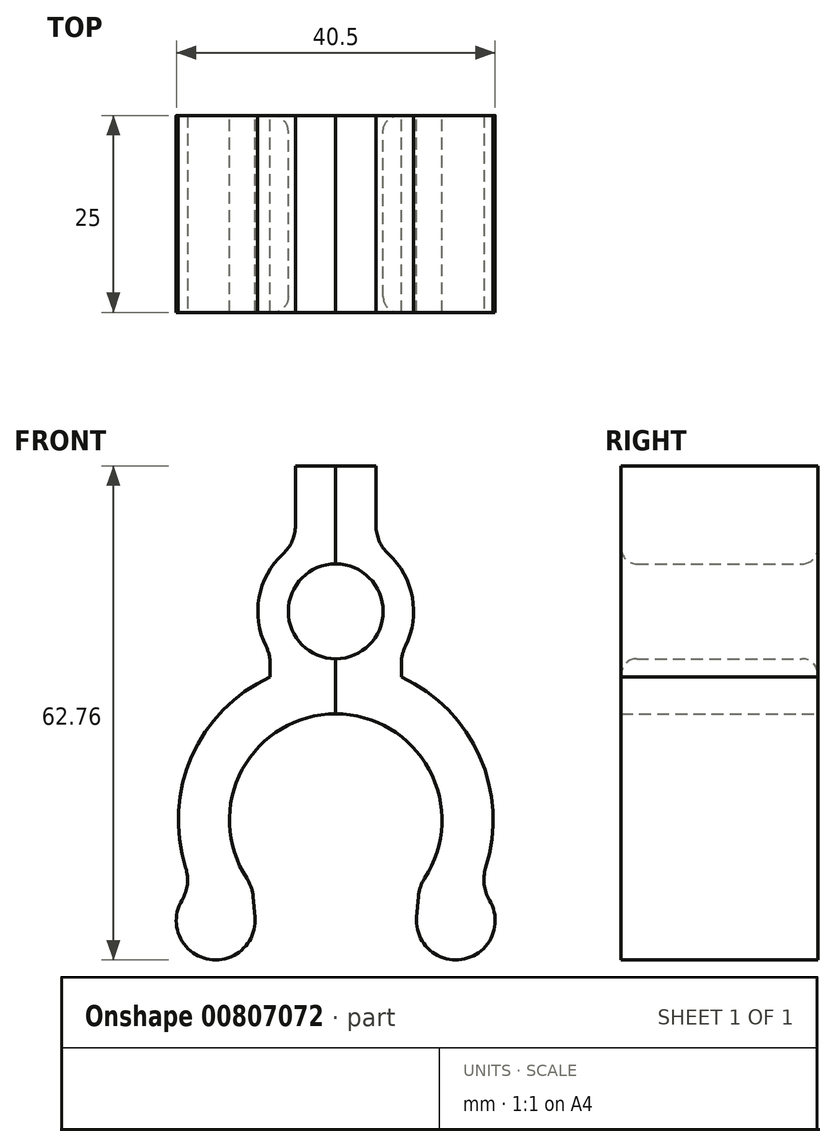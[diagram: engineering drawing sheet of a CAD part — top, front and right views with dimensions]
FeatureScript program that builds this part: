
annotation { "Feature Type Name" : "Feature", "Feature Type Description" : "" }
export const myFeature = defineFeature(function(context is Context, id is Id, definition is map)
    precondition{}
    {
        {
            var Q0;
            Q0=qCreatedBy(makeId("Front.planeOp"),FACE);
            var sketch = newSketch(context, id + "F0", { "sketchPlane" : qUnion([Q0])});
            skLineSegment(sketch, "E0", {"start": v(10.61, -34.87) * mm, "end": v(10.27, -38.85) * mm});
            skArc(sketch, "E1", {"start": v(10.27, -38.85) * mm, "mid": v(17.41, -43.8) * mm, "end": v(18.05, -35.14) * mm});
            skArc(sketch, "E2", {"start": v(8.33, -5.34) * mm, "mid": v(9.64, 2.25) * mm, "end": v(5.11, 8.48) * mm});
            skArc(sketch, "E3", {"start": v(0, -6.02) * mm, "mid": v(6.02, 0) * mm, "end": v(0, 6.02) * mm});
            skPoint(sketch, "E4.end.orphan", {"position": v(5.11, 0) * mm});
            skLineSegment(sketch, "E5", {"start": v(0, 71.13) * mm, "end": v(0, -72.93) * mm, "construction": true});
            skLineSegment(sketch, "E6", {"start": v(5.11, 8.48) * mm, "end": v(5.11, 18.48) * mm});
            skLineSegment(sketch, "E7", {"start": v(0.13, 84.1) * mm, "end": v(0, 71.13) * mm, "construction": true});
            skLineSegment(sketch, "E8", {"start": v(5.11, 18.48) * mm, "end": v(0, 18.48) * mm});
            skLineSegment(sketch, "E9", {"start": v(0, 18.48) * mm, "end": v(0, 6.02) * mm});
            skLineSegment(sketch, "E10", {"start": v(0, -6.02) * mm, "end": v(0, -26.52) * mm});
            skArc(sketch, "E11", {"start": v(10.61, -34.87) * mm, "mid": v(12.14, -20.63) * mm, "end": v(0, -13.02) * mm});
            skLineSegment(sketch, "E12", {"start": v(8.33, -5.34) * mm, "end": v(8.33, -8.34) * mm});
            skArc(sketch, "E13", {"start": v(18.05, -35.14) * mm, "mid": v(18.8, -19.7) * mm, "end": v(8.33, -8.34) * mm});
            skSolve(sketch);
        }
        {
            var Q0;
            Q0=qSketchRegion(id+"F0",true);
            extrude(context, id + "F1", {"entities" : qUnion([Q0]), "depth" : 25 * mm, "offsetDistance" : 25 * mm});
        }
        {
            var Q0;
            Q0=makeQuery(id+"F1.opExtrude","SWEPT_BODY",BODY,{"disambiguationData":[OSD([sQuery(id+"F0.wireOp",EDGE,"cfabb739-dba9-4975-bd49-091e3b57f569"),sQuery(id+"F0.wireOp",EDGE,"5847780e-0f5a-4472-9120-1fdb006a39dd"),sQuery(id+"F0.wireOp",EDGE,"E0"),sQuery(id+"F0.wireOp",EDGE,"E1"),sQuery(id+"F0.wireOp",EDGE,"E2"),sQuery(id+"F0.wireOp",EDGE,"E3"),sQuery(id+"F0.wireOp",EDGE,"LwMaPAxc-ASng-TWKL-FKsP-XUbiFX4LCitD"),sQuery(id+"F0.wireOp",EDGE,"E6"),sQuery(id+"F0.wireOp",EDGE,"E8"),sQuery(id+"F0.wireOp",EDGE,"E9"),sQuery(id+"F0.wireOp",EDGE,"E10")])]});
            var Q1;
            Q1=qCreatedBy(makeId("Right.planeOp"),FACE);
            mirror(context, id + "F2", {"entities" : qUnion([Q0]), "mirrorPlane" : qUnion([Q1])});
        }
        {
            var Q0;
            Q0=makeQuery(id+"F1.opExtrude","SWEPT_EDGE",EDGE,{"disambiguationData":[OSD([sQuery(id+"F0.wireOp",EDGE,"E0"),sQuery(id+"F0.wireOp",EDGE,"E11")])]});
            var Q1;
            Q1=makeQuery(id+"F2.opPattern","COPY",EDGE,{"derivedFrom":makeQuery(id+"F1.opExtrude","SWEPT_EDGE",EDGE,{"disambiguationData":[OSD([sQuery(id+"F0.wireOp",EDGE,"E0"),sQuery(id+"F0.wireOp",EDGE,"E11")])]}),"instanceName":"1"});
            var Q2;
            Q2=makeQuery(id+"F2.opPattern","COPY",EDGE,{"derivedFrom":makeQuery(id+"F1.opExtrude","SWEPT_EDGE",EDGE,{"disambiguationData":[OSD([sQuery(id+"F0.wireOp",EDGE,"E1"),sQuery(id+"F0.wireOp",EDGE,"E13")])]}),"instanceName":"1"});
            var Q3;
            Q3=makeQuery(id+"F1.opExtrude","SWEPT_EDGE",EDGE,{"disambiguationData":[OSD([sQuery(id+"F0.wireOp",EDGE,"E1"),sQuery(id+"F0.wireOp",EDGE,"E13")])]});
            var Q4;
            Q4=makeQuery(id+"F2.opPattern","COPY",EDGE,{"derivedFrom":makeQuery(id+"F1.opExtrude","SWEPT_EDGE",EDGE,{"disambiguationData":[OSD([sQuery(id+"F0.wireOp",EDGE,"E2"),sQuery(id+"F0.wireOp",EDGE,"E6")])]}),"instanceName":"1"});
            var Q5;
            Q5=makeQuery(id+"F2.opPattern","COPY",EDGE,{"derivedFrom":makeQuery(id+"F1.opExtrude","SWEPT_EDGE",EDGE,{"disambiguationData":[OSD([sQuery(id+"F0.wireOp",EDGE,"E2"),sQuery(id+"F0.wireOp",EDGE,"E12")])]}),"instanceName":"1"});
            var Q6;
            Q6=makeQuery(id+"F1.opExtrude","SWEPT_EDGE",EDGE,{"disambiguationData":[OSD([sQuery(id+"F0.wireOp",EDGE,"E2"),sQuery(id+"F0.wireOp",EDGE,"E6")])]});
            var Q7;
            Q7=makeQuery(id+"F1.opExtrude","SWEPT_EDGE",EDGE,{"disambiguationData":[OSD([sQuery(id+"F0.wireOp",EDGE,"E2"),sQuery(id+"F0.wireOp",EDGE,"E12")])]});
            var Q8;
            Q8=makeQuery(id+"F2.opPattern","COPY",EDGE,{"derivedFrom":makeQuery(id+"Fz5VlACo7VjdTQA_1.opExtrude","SWEPT_EDGE",EDGE,{"disambiguationData":[OSD([sQuery(id+"FI2dAfJpOKtGOTZ_1.wireOp",EDGE,"UufLFT2Z-upBZ-YC00-3sW9-ZrS4UPln2tA3"),sQuery(id+"FI2dAfJpOKtGOTZ_1.wireOp",EDGE,"f7488829-f30d-4c1d-9d05-a88ade316224.trimOffspring")])]}),"instanceName":"1"});
            var Q9;
            Q9=makeQuery(id+"F2.opPattern","COPY",EDGE,{"derivedFrom":makeQuery(id+"Fz5VlACo7VjdTQA_1.opExtrude","SWEPT_EDGE",EDGE,{"disambiguationData":[OSD([sQuery(id+"FI2dAfJpOKtGOTZ_1.wireOp",EDGE,"82edda89-2339-4690-89e7-abee45e1404a.trimOffspring"),sQuery(id+"FI2dAfJpOKtGOTZ_1.wireOp",EDGE,"e6c82897-9f81-4bd0-b549-450949e90f70.trimOffspring")])]}),"instanceName":"1"});
            var Q10;
            Q10=makeQuery(id+"F2.opPattern","COPY",EDGE,{"derivedFrom":makeQuery(id+"Fz5VlACo7VjdTQA_1.opExtrude","SWEPT_EDGE",EDGE,{"disambiguationData":[OSD([sQuery(id+"FI2dAfJpOKtGOTZ_1.wireOp",EDGE,"dAwRz9Mk-8VAy-pzP0-fNDg-vniHaInSBWGX"),sQuery(id+"FI2dAfJpOKtGOTZ_1.wireOp",EDGE,"3f8ad037-8f99-422e-a5f7-4226f7c6d37a0.MirrorCS")])]}),"instanceName":"1"});
            var Q11;
            Q11=makeQuery(id+"Fz5VlACo7VjdTQA_1.opExtrude","SWEPT_EDGE",EDGE,{"disambiguationData":[OSD([sQuery(id+"FI2dAfJpOKtGOTZ_1.wireOp",EDGE,"dAwRz9Mk-8VAy-pzP0-fNDg-vniHaInSBWGX"),sQuery(id+"FI2dAfJpOKtGOTZ_1.wireOp",EDGE,"o45zF1qc-RgXT-cvMq-ReTE-ZHE0aTBPM8XX")])]});
            fillet(context, id + "F3", {"entities" : qUnion([Q0, Q1, Q2, Q3, Q4, Q5, Q6, Q7, Q8, Q9, Q10, Q11]), "radius" : 5 * mm, "tangentPropagation" : true, "allowEdgeOverflow" : false});
        }
        {
            var Q0;
            Q0=makeQuery(id+"F1.opExtrude","CAP_EDGE",EDGE,{"disambiguationData":[OSD([sQuery(id+"F0.wireOp",EDGE,"E3")])],"isStart":false});
            var Q1;
            Q1=makeQuery(id+"F2.opPattern","COPY",EDGE,{"derivedFrom":makeQuery(id+"F1.opExtrude","CAP_EDGE",EDGE,{"disambiguationData":[OSD([sQuery(id+"F0.wireOp",EDGE,"E3")])],"isStart":false}),"instanceName":"1"});
            var Q2;
            Q2=makeQuery(id+"F2.opPattern","COPY",EDGE,{"derivedFrom":makeQuery(id+"F1.opExtrude","CAP_EDGE",EDGE,{"disambiguationData":[OSD([sQuery(id+"F0.wireOp",EDGE,"E3")])],"isStart":true}),"instanceName":"1"});
            var Q3;
            Q3=makeQuery(id+"F1.opExtrude","CAP_EDGE",EDGE,{"disambiguationData":[OSD([sQuery(id+"F0.wireOp",EDGE,"E3")])],"isStart":true});
            var Q4;
            Q4=makeQuery(id+"F2.opPattern","COPY",EDGE,{"derivedFrom":makeQuery(id+"Fz5VlACo7VjdTQA_1.opExtrude","CAP_EDGE",EDGE,{"disambiguationData":[OSD([sQuery(id+"F0.wireOp",EDGE,"E6"),sQuery(id+"F0.wireOp",EDGE,"E8")])],"isStart":false}),"instanceName":"1"});
            var Q5;
            Q5=makeQuery(id+"Fz5VlACo7VjdTQA_1.opExtrude","CAP_EDGE",EDGE,{"disambiguationData":[OSD([sQuery(id+"F0.wireOp",EDGE,"E6"),sQuery(id+"F0.wireOp",EDGE,"E8")])],"isStart":false});
            fillet(context, id + "F4", {"entities" : qUnion([Q0, Q1, Q2, Q3, Q4, Q5]), "radius" : 2 * mm, "tangentPropagation" : true, "allowEdgeOverflow" : false});
        }
    });
